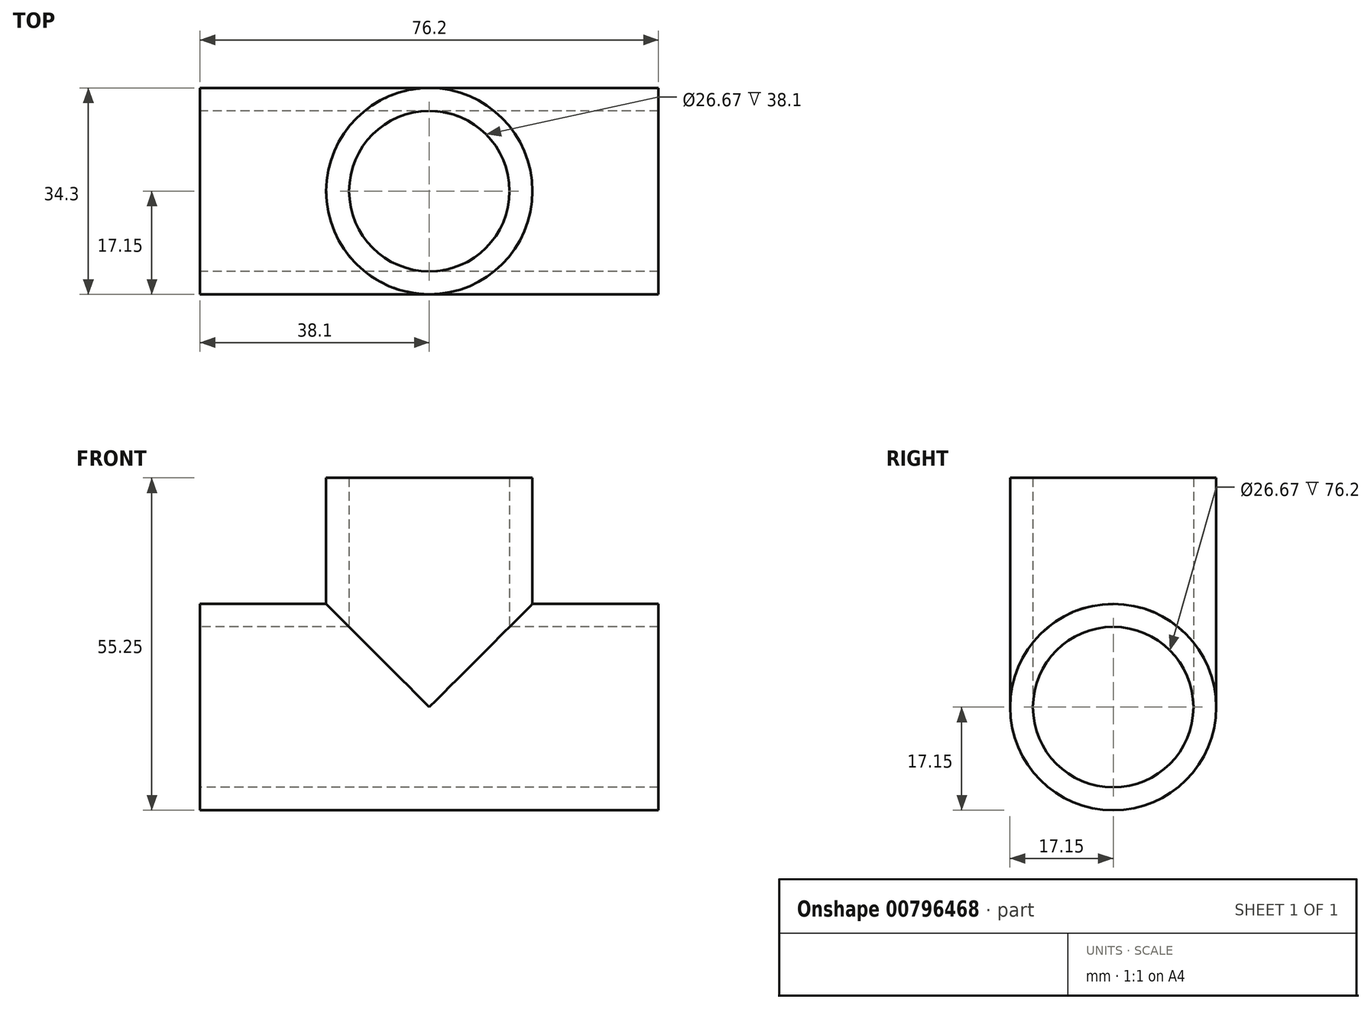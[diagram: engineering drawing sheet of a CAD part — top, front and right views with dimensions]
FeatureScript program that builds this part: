
annotation { "Feature Type Name" : "Feature", "Feature Type Description" : "" }
export const myFeature = defineFeature(function(context is Context, id is Id, definition is map)
    precondition{}
    {
        {
            var Q0;
            Q0=qCreatedBy(makeId("Right.planeOp"),FACE);
            var sketch = newSketch(context, id + "F0", { "sketchPlane" : qUnion([Q0])});
            skCircle(sketch, "E0", {"center": v(0, 0) * mm, "radius": 13.34 * mm});
            skCircle(sketch, "E1.0", {"center": v(0, 0) * mm, "radius": 17.14 * mm});
            skSolve(sketch);
        }
        {
            var Q0;
            Q0 = qSketchRegion(id + "F0", true);
            extrude(context, id + "F1", {"entities" : qUnion([Q0]), "depth" : 76.2 * mm, "offsetDistance" : 25.4 * mm});
        }
        {
            var Q0;
            Q0=qCreatedBy(makeId("Right.planeOp"),FACE);
            var sketch = newSketch(context, id + "F2", { "sketchPlane" : qUnion([Q0])});
            skCircle(sketch, "E2", {"center": v(0, 0) * mm, "radius": 13.34 * mm});
            skSolve(sketch);
        }
        {
            var Q0;
            Q0=qCreatedBy(makeId("Top.planeOp"),FACE);
            var sketch = newSketch(context, id + "F3", { "sketchPlane" : qUnion([Q0])});
            skLineSegment(sketch, "E3", {"start": v(0, 0) * mm, "end": v(38.1, 0) * mm});
            skCircle(sketch, "E4", {"center": v(38.1, 0) * mm, "radius": 13.34 * mm});
            skCircle(sketch, "E5.0", {"center": v(38.1, 0) * mm, "radius": 17.14 * mm});
            skSolve(sketch);
        }
        {
            var Q0;
            Q0 = qSketchRegion(id + "F3", true);
            extrude(context, id + "F4", {"entities" : qUnion([Q0]), "operationType" : NewBodyOperationType.ADD, "depth" : 38.1 * mm, "offsetDistance" : 25.4 * mm});
        }
        {
            var Q0;
            Q0=qCreatedBy(makeId("Top.planeOp"),FACE);
            var sketch = newSketch(context, id + "F5", { "sketchPlane" : qUnion([Q0])});
            skLineSegment(sketch, "E6", {"start": v(0, 0) * mm, "end": v(38.1, 0) * mm});
            skCircle(sketch, "E7", {"center": v(38.1, 0) * mm, "radius": 13.34 * mm});
            skSolve(sketch);
        }
        {
            var Q0;
            Q0=sQuery(id+"F5.wireOp",VERTEX,"E6.end");
            var Q1;
            Q1=makeQuery(id+"F1.opExtrude","SWEPT_BODY",BODY,{"disambiguationData":[OSD([sQuery(id+"F0.wireOp",EDGE,"E0"),sQuery(id+"F0.wireOp",EDGE,"E1.0")])]});
            hole(context, id + "F6", {"style" : HoleStyle.SIMPLE, "endStyle" : HoleEndStyle.THROUGH, "oppositeDirection" : true, "holeDiameter" : 26.67 * mm, "majorDiameter" : 6.35 * mm, "isTappedThrough" : true, "tappedDepth" : 12.7 * mm, "tapClearance" : 3, "locations" : qUnion([Q0]), "scope" : qUnion([Q1])});
        }
        {
            var Q0;
            Q0=sQuery(id+"F2.wireOp",VERTEX,"E2.center");
            var Q1;
            Q1=makeQuery(id+"F1.opExtrude","SWEPT_BODY",BODY,{"disambiguationData":[OSD([sQuery(id+"F0.wireOp",EDGE,"E0"),sQuery(id+"F0.wireOp",EDGE,"E1.0")])]});
            hole(context, id + "F7", {"style" : HoleStyle.SIMPLE, "endStyle" : HoleEndStyle.THROUGH, "oppositeDirection" : true, "holeDiameter" : 26.67 * mm, "majorDiameter" : 6.35 * mm, "isTappedThrough" : true, "tappedDepth" : 12.7 * mm, "tapClearance" : 3, "locations" : qUnion([Q0]), "scope" : qUnion([Q1])});
        }
    });
